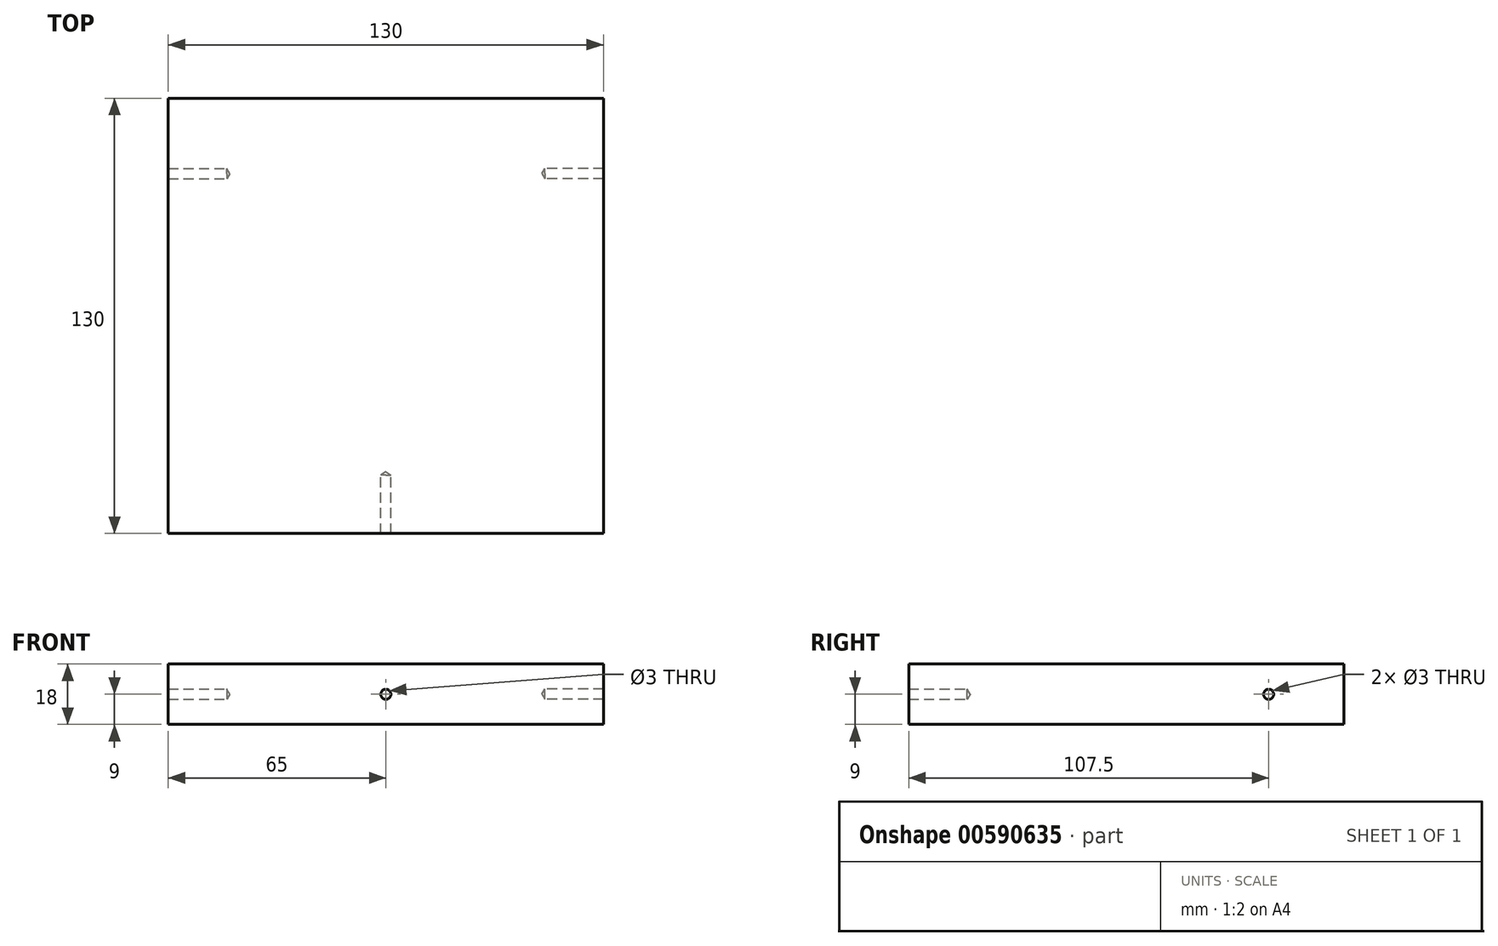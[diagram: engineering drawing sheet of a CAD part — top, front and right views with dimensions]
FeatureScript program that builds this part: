
annotation { "Feature Type Name" : "Feature", "Feature Type Description" : "" }
export const myFeature = defineFeature(function(context is Context, id is Id, definition is map)
    precondition{}
    {
        {
            var Q0;
            Q0=qCreatedBy(makeId("Top.planeOp"),FACE);
            var sketch = newSketch(context, id + "F0", { "sketchPlane" : qUnion([Q0])});
            skLineSegment(sketch, "E0.bottom", {"start": v(55, 65) * mm, "end": v(-55, 65) * mm});
            skLineSegment(sketch, "E0.top", {"start": v(55, -65) * mm, "end": v(-55, -65) * mm});
            skLineSegment(sketch, "E0.left", {"start": v(65, 55) * mm, "end": v(65, -55) * mm});
            skLineSegment(sketch, "E0.right", {"start": v(-65, 55) * mm, "end": v(-65, -55) * mm});
            skPoint(sketch, "E1.orphan", {"position": v(-65, 65) * mm});
            skPoint(sketch, "E2.orphan", {"position": v(65, 65) * mm});
            skPoint(sketch, "E3.orphan", {"position": v(65, -65) * mm});
            skPoint(sketch, "E4.orphan", {"position": v(-65, -65) * mm});
            skLineSegment(sketch, "E5", {"start": v(-65, 55) * mm, "end": v(-65, 65) * mm});
            skLineSegment(sketch, "E6", {"start": v(-65, 65) * mm, "end": v(-55, 65) * mm});
            skLineSegment(sketch, "E7", {"start": v(55, 65) * mm, "end": v(65, 65) * mm});
            skLineSegment(sketch, "E8", {"start": v(65, 65) * mm, "end": v(65, 55) * mm});
            skLineSegment(sketch, "E9", {"start": v(-65, -55) * mm, "end": v(-65, -65) * mm});
            skLineSegment(sketch, "E10", {"start": v(-65, -65) * mm, "end": v(-55, -65) * mm});
            skLineSegment(sketch, "E11", {"start": v(55, -65) * mm, "end": v(65, -65) * mm});
            skLineSegment(sketch, "E12", {"start": v(65, -65) * mm, "end": v(65, -55) * mm});
            skSolve(sketch);
        }
        {
            var Q0;
            Q0=makeQuery(id+"F0.imprint","IMPRINT",FACE,{"disambiguationData":[TD([[makeQuery(id+"F0.imprint","IMPRINT",EDGE,{"derivedFrom":sQuery(id+"F0.wireOp",EDGE,"E0.bottom")}),1.0]])]});
            extrude(context, id + "F1", {"entities" : qUnion([Q0]), "depth" : 18 * mm, "offsetDistance" : 25 * mm});
        }
        {
            var Q0;
            Q0=makeQuery(id+"F1.opExtrude","SWEPT_FACE",FACE,{"disambiguationData":[OSD([sQuery(id+"F0.wireOp",EDGE,"E0.top")])]});
            var sketch = newSketch(context, id + "F2", { "sketchPlane" : qUnion([Q0])});
            skPoint(sketch, "E13", {"position": v(0, 9) * mm});
            skPoint(sketch, "E14", {"position": v(0, 18) * mm});
            skPoint(sketch, "E15", {"position": v(-65, 9) * mm});
            skSolve(sketch);
        }
        {
            var Q0;
            Q0=sQuery(id+"F2.wireOp",VERTEX,"E13");
            var Q1;
            Q1=makeQuery(id+"F1.opExtrude","SWEPT_BODY",BODY,{"disambiguationData":[OSD([sQuery(id+"F0.wireOp",EDGE,"E0.bottom"),sQuery(id+"F0.wireOp",EDGE,"E0.top"),sQuery(id+"F0.wireOp",EDGE,"E0.left"),sQuery(id+"F0.wireOp",EDGE,"E0.right"),sQuery(id+"F0.wireOp",EDGE,"533qQTwQ-isX0-n8Dz-8QbI-yUsE9O27EQTo"),sQuery(id+"F0.wireOp",EDGE,"d8f7d482-ad02-4c13-8fa5-89a314720c870.MirrorCS"),sQuery(id+"F0.wireOp",EDGE,"e57d2cfa-8b82-42a2-a3a3-33eb06e36f430.MirrorCS"),sQuery(id+"F0.wireOp",EDGE,"05644432-93e5-4c25-9c1b-29d9b73179a90.MirrorCS")])]});
            hole(context, id + "F3", {"style" : HoleStyle.SIMPLE, "endStyle" : HoleEndStyle.BLIND, "holeDiameter" : 3 * mm, "majorDiameter" : 5 * mm, "holeDepth" : 17.5 * mm, "isTappedThrough" : true, "tappedDepth" : 12 * mm, "tapClearance" : 3, "locations" : qUnion([Q0]), "scope" : qUnion([Q1])});
        }
        {
            var Q0;
            Q0=makeQuery(id+"F1.opExtrude","SWEPT_FACE",FACE,{"disambiguationData":[OSD([sQuery(id+"F0.wireOp",EDGE,"E0.left")])]});
            var sketch = newSketch(context, id + "F4", { "sketchPlane" : qUnion([Q0])});
            skPoint(sketch, "E16", {"position": v(42.5, 9) * mm});
            skSolve(sketch);
        }
        {
            var Q0;
            Q0=sQuery(id+"F4.wireOp",VERTEX,"E16");
            var Q1;
            Q1=makeQuery(id+"F1.opExtrude","SWEPT_BODY",BODY,{"disambiguationData":[OSD([sQuery(id+"F0.wireOp",EDGE,"E0.bottom"),sQuery(id+"F0.wireOp",EDGE,"E0.top"),sQuery(id+"F0.wireOp",EDGE,"E0.left"),sQuery(id+"F0.wireOp",EDGE,"E0.right"),sQuery(id+"F0.wireOp",EDGE,"533qQTwQ-isX0-n8Dz-8QbI-yUsE9O27EQTo"),sQuery(id+"F0.wireOp",EDGE,"d8f7d482-ad02-4c13-8fa5-89a314720c870.MirrorCS"),sQuery(id+"F0.wireOp",EDGE,"e57d2cfa-8b82-42a2-a3a3-33eb06e36f430.MirrorCS"),sQuery(id+"F0.wireOp",EDGE,"05644432-93e5-4c25-9c1b-29d9b73179a90.MirrorCS")])]});
            hole(context, id + "F5", {"style" : HoleStyle.SIMPLE, "endStyle" : HoleEndStyle.BLIND, "holeDiameter" : 3 * mm, "majorDiameter" : 5 * mm, "holeDepth" : 17.5 * mm, "isTappedThrough" : true, "tappedDepth" : 12 * mm, "tapClearance" : 3, "locations" : qUnion([Q0]), "scope" : qUnion([Q1])});
        }
        {
            var Q0;
            Q0=makeQuery(id+"F1.opExtrude","SWEPT_FACE",FACE,{"disambiguationData":[OSD([sQuery(id+"F0.wireOp",EDGE,"E0.right")])]});
            var sketch = newSketch(context, id + "F6", { "sketchPlane" : qUnion([Q0])});
            skPoint(sketch, "E17", {"position": v(-42.5, 9) * mm});
            skPoint(sketch, "E18", {"position": v(-65, 9) * mm});
            skSolve(sketch);
        }
        {
            var Q0;
            Q0=sQuery(id+"F6.wireOp",VERTEX,"E17");
            var Q1;
            Q1=makeQuery(id+"F1.opExtrude","SWEPT_BODY",BODY,{"disambiguationData":[OSD([sQuery(id+"F0.wireOp",EDGE,"E0.bottom"),sQuery(id+"F0.wireOp",EDGE,"E0.top"),sQuery(id+"F0.wireOp",EDGE,"E0.left"),sQuery(id+"F0.wireOp",EDGE,"E0.right"),sQuery(id+"F0.wireOp",EDGE,"533qQTwQ-isX0-n8Dz-8QbI-yUsE9O27EQTo"),sQuery(id+"F0.wireOp",EDGE,"d8f7d482-ad02-4c13-8fa5-89a314720c870.MirrorCS"),sQuery(id+"F0.wireOp",EDGE,"e57d2cfa-8b82-42a2-a3a3-33eb06e36f430.MirrorCS"),sQuery(id+"F0.wireOp",EDGE,"05644432-93e5-4c25-9c1b-29d9b73179a90.MirrorCS")])]});
            hole(context, id + "F7", {"style" : HoleStyle.SIMPLE, "endStyle" : HoleEndStyle.BLIND, "holeDiameter" : 3 * mm, "majorDiameter" : 5 * mm, "holeDepth" : 17.5 * mm, "isTappedThrough" : true, "tappedDepth" : 12 * mm, "tapClearance" : 3, "locations" : qUnion([Q0]), "scope" : qUnion([Q1])});
        }
    });
